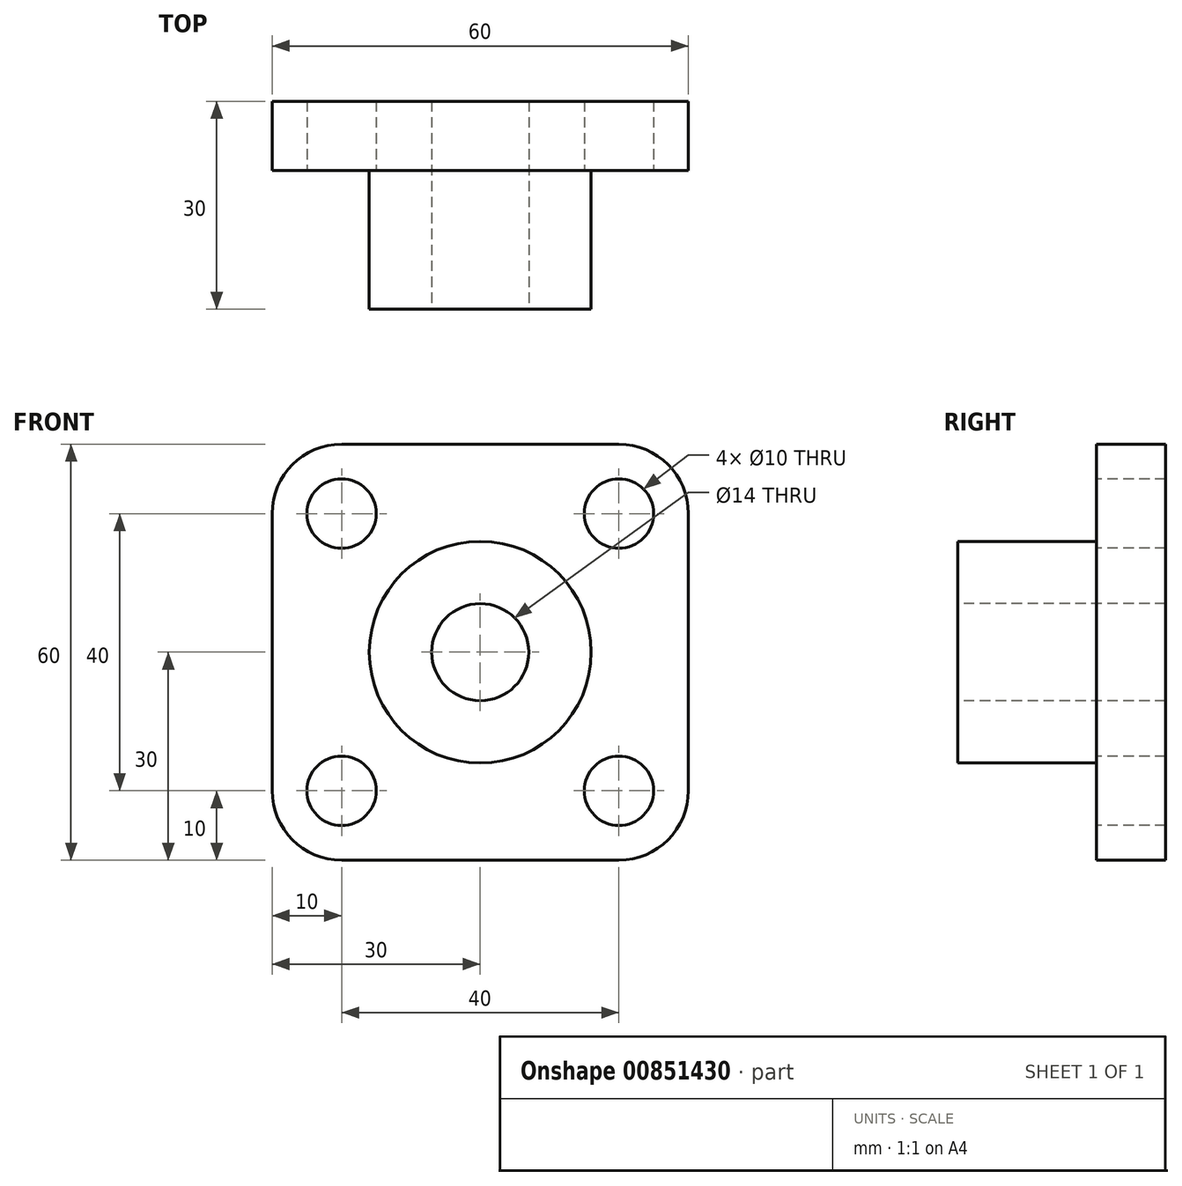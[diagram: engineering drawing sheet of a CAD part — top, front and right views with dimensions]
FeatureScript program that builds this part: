
annotation { "Feature Type Name" : "Feature", "Feature Type Description" : "" }
export const myFeature = defineFeature(function(context is Context, id is Id, definition is map)
    precondition{}
    {
        {
            var Q0;
            Q0=qCreatedBy(makeId("Front.planeOp"),FACE);
            var sketch = newSketch(context, id + "F0", { "sketchPlane" : qUnion([Q0])});
            skLineSegment(sketch, "E0.bottom", {"start": v(30, 30) * mm, "end": v(-30, 30) * mm});
            skLineSegment(sketch, "E0.top", {"start": v(30, -30) * mm, "end": v(-30, -30) * mm});
            skLineSegment(sketch, "E0.left", {"start": v(30, 30) * mm, "end": v(30, -30) * mm});
            skLineSegment(sketch, "E0.right", {"start": v(-30, 30) * mm, "end": v(-30, -30) * mm});
            skPoint(sketch, "E0.middle", {"position": v(0, 0) * mm});
            skLineSegment(sketch, "E1", {"start": v(-20, 39.76) * mm, "end": v(-20, -51.97) * mm, "construction": true});
            skLineSegment(sketch, "E2", {"start": v(20, -51.97) * mm, "end": v(20, 50.37) * mm, "construction": true});
            skLineSegment(sketch, "E3", {"start": v(-59.74, 20) * mm, "end": v(58.34, 20) * mm, "construction": true});
            skLineSegment(sketch, "E4", {"start": v(54.92, -20) * mm, "end": v(-69.32, -20) * mm, "construction": true});
            skPoint(sketch, "E5", {"position": v(-20, 20) * mm});
            skPoint(sketch, "E6", {"position": v(20, 20) * mm});
            skPoint(sketch, "E7", {"position": v(20, -20) * mm});
            skPoint(sketch, "E8", {"position": v(-20, -20) * mm});
            skSolve(sketch);
        }
        {
            var Q0;
            Q0=makeQuery(id+"F0.imprint","IMPRINT",FACE,{"disambiguationData":[TD([[makeQuery(id+"F0.imprint","IMPRINT",EDGE,{"derivedFrom":sQuery(id+"F0.wireOp",EDGE,"E0.bottom")}),1.0]])]});
            extrude(context, id + "F1", {"entities" : qUnion([Q0]), "depth" : 10 * mm, "offsetDistance" : 25 * mm});
        }
        {
            var Q0;
            Q0=makeQuery(id+"F1.opExtrude","SWEPT_EDGE",EDGE,{"disambiguationData":[OSD([sQuery(id+"F0.wireOp",EDGE,"E0.bottom"),sQuery(id+"F0.wireOp",EDGE,"E0.right")])]});
            var Q1;
            Q1=makeQuery(id+"F1.opExtrude","SWEPT_EDGE",EDGE,{"disambiguationData":[OSD([sQuery(id+"F0.wireOp",EDGE,"E0.top"),sQuery(id+"F0.wireOp",EDGE,"E0.right")])]});
            var Q2;
            Q2=makeQuery(id+"F1.opExtrude","SWEPT_EDGE",EDGE,{"disambiguationData":[OSD([sQuery(id+"F0.wireOp",EDGE,"E0.bottom"),sQuery(id+"F0.wireOp",EDGE,"E0.left")])]});
            var Q3;
            Q3=makeQuery(id+"F1.opExtrude","SWEPT_EDGE",EDGE,{"disambiguationData":[OSD([sQuery(id+"F0.wireOp",EDGE,"E0.top"),sQuery(id+"F0.wireOp",EDGE,"E0.left")])]});
            fillet(context, id + "F2", {"entities" : qUnion([Q0, Q1, Q2, Q3]), "radius" : 10 * mm, "tangentPropagation" : true, "allowEdgeOverflow" : false});
        }
        {
            var Q0;
            Q0=makeQuery(id+"F1.opExtrude","CAP_FACE",FACE,{"disambiguationData":[OSD([sQuery(id+"F0.wireOp",EDGE,"E0.bottom"),sQuery(id+"F0.wireOp",EDGE,"E0.top"),sQuery(id+"F0.wireOp",EDGE,"E0.left"),sQuery(id+"F0.wireOp",EDGE,"E0.right")])],"isStart":false});
            var sketch = newSketch(context, id + "F3", { "sketchPlane" : qUnion([Q0])});
            skLineSegment(sketch, "E9", {"start": v(-20, 36.13) * mm, "end": v(-20, -43.73) * mm, "construction": true});
            skLineSegment(sketch, "E10", {"start": v(20, -43.73) * mm, "end": v(20, 41.94) * mm, "construction": true});
            skLineSegment(sketch, "E11", {"start": v(-47.03, 20) * mm, "end": v(47.6, 20) * mm, "construction": true});
            skLineSegment(sketch, "E12", {"start": v(43.49, -20) * mm, "end": v(-68.08, -20) * mm, "construction": true});
            skPoint(sketch, "E13", {"position": v(-20, 20) * mm});
            skPoint(sketch, "E14", {"position": v(20, 20) * mm});
            skPoint(sketch, "E15", {"position": v(20, -20) * mm});
            skPoint(sketch, "E16", {"position": v(-20, -20) * mm});
            skSolve(sketch);
        }
        {
            var Q0;
            Q0=sQuery(id+"F3.wireOp",VERTEX,"E13");
            var Q1;
            Q1=sQuery(id+"F3.wireOp",VERTEX,"E14");
            var Q2;
            Q2=sQuery(id+"F3.wireOp",VERTEX,"E15");
            var Q3;
            Q3=sQuery(id+"F3.wireOp",VERTEX,"E16");
            var Q4;
            Q4=makeQuery(id+"F1.opExtrude","SWEPT_BODY",BODY,{"disambiguationData":[OSD([sQuery(id+"F0.wireOp",EDGE,"E0.bottom"),sQuery(id+"F0.wireOp",EDGE,"E0.top"),sQuery(id+"F0.wireOp",EDGE,"E0.left"),sQuery(id+"F0.wireOp",EDGE,"E0.right")])]});
            hole(context, id + "F4", {"style" : HoleStyle.SIMPLE, "endStyle" : HoleEndStyle.THROUGH, "holeDiameter" : 10 * mm, "majorDiameter" : 5 * mm, "isTappedThrough" : true, "tappedDepth" : 19 * mm, "tapClearance" : 3, "locations" : qUnion([Q0, Q1, Q2, Q3]), "scope" : qUnion([Q4])});
        }
        {
            var Q0;
            Q0=makeQuery(id+"F1.opExtrude","CAP_FACE",FACE,{"disambiguationData":[OSD([sQuery(id+"F0.wireOp",EDGE,"E0.bottom"),sQuery(id+"F0.wireOp",EDGE,"E0.top"),sQuery(id+"F0.wireOp",EDGE,"E0.left"),sQuery(id+"F0.wireOp",EDGE,"E0.right")])],"isStart":false});
            var sketch = newSketch(context, id + "F5", { "sketchPlane" : qUnion([Q0])});
            skCircle(sketch, "E17", {"center": v(0, 0) * mm, "radius": 16 * mm});
            skSolve(sketch);
        }
        {
            var Q0;
            Q0=makeQuery(id+"F5.imprint","IMPRINT",FACE,{"disambiguationData":[TD([[makeQuery(id+"F5.imprint","IMPRINT",EDGE,{"derivedFrom":sQuery(id+"F5.wireOp",EDGE,"E17")}),1.0]])]});
            extrude(context, id + "F6", {"entities" : qUnion([Q0]), "operationType" : NewBodyOperationType.ADD, "depth" : 20 * mm, "offsetDistance" : 25 * mm});
        }
        {
            var Q0;
            Q0=makeQuery(id+"F6.opExtrude","CAP_FACE",FACE,{"disambiguationData":[OSD([sQuery(id+"F5.wireOp",EDGE,"E17")])],"isStart":false});
            var sketch = newSketch(context, id + "F7", { "sketchPlane" : qUnion([Q0])});
            skPoint(sketch, "E18", {"position": v(0, 0) * mm});
            skSolve(sketch);
        }
        {
            var Q0;
            Q0=sQuery(id+"F7.wireOp",VERTEX,"E18");
            var Q1;
            Q1=makeQuery(id+"F1.opExtrude","SWEPT_BODY",BODY,{"disambiguationData":[OSD([sQuery(id+"F0.wireOp",EDGE,"E0.bottom"),sQuery(id+"F0.wireOp",EDGE,"E0.top"),sQuery(id+"F0.wireOp",EDGE,"E0.left"),sQuery(id+"F0.wireOp",EDGE,"E0.right")])]});
            hole(context, id + "F8", {"style" : HoleStyle.SIMPLE, "endStyle" : HoleEndStyle.THROUGH, "standardTappedOrClearance" : lookupTablePath({ "standard" : "ISO", "engagement" : "75%", "pitch" : "2 mm", "size" : "M16", "type" : "Tapped" }), "standardBlindInLast" : lookupTablePath({ "standard" : "ISO", "engagement" : "75%", "pitch" : "2 mm", "size" : "M16", "type" : "Tapped" }), "holeDiameter" : 14 * mm, "majorDiameter" : 16 * mm, "showTappedDepth" : true, "isTappedThrough" : true, "tappedDepth" : 19 * mm, "tapClearance" : 3, "locations" : qUnion([Q0]), "scope" : qUnion([Q1])});
        }
    });
